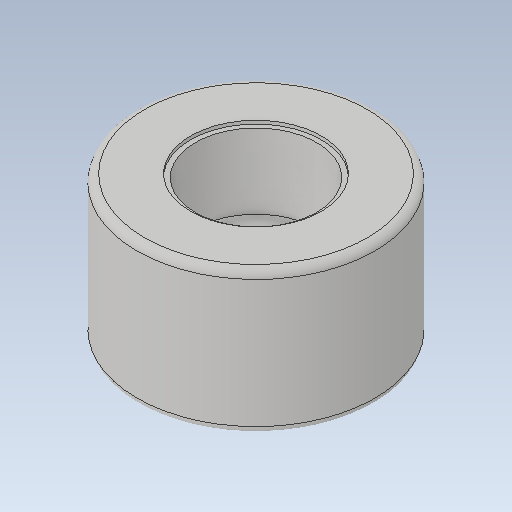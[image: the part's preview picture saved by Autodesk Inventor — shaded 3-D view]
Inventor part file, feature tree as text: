
AUTODESK INVENTOR PART (.ipt)
format: ipt  version: 2021 (Build 250183000, 183)  size: 180,224 bytes
history: native  units: in
note: dims shown in document units (in); Inventor stores cm internally (conversion verified against a paired STEP export)
features: fillet x1
ambient origin geometry x8: Origin, YZ Plane, XZ Plane, XY Plane, X Axis, Y Axis, Z Axis, Center Point
bodies: Solid1 (feature_tree)
feature tree (1):
  fillet  "Fillet1"  [1 undecoded]
note: 1 required parameter value undecoded (feature->parameter linkage not recoverable at this tier; creation-order binding heuristic only, values carry confidence <= 0.55)
